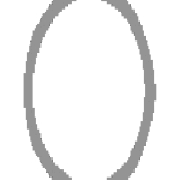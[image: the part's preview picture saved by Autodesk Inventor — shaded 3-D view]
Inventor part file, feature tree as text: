
AUTODESK INVENTOR PART (.ipt)
format: ipt  version: 2021 (Build 250183000, 183)  size: 113,152 bytes
history: native  units: in
note: dims shown in document units (in); Inventor stores cm internally (conversion verified against a paired STEP export)
features: other x4, sketch x3, plane x1
ambient origin geometry x8: Origin, YZ Plane, XZ Plane, XY Plane, X Axis, Y Axis, Z Axis, Center Point
bodies: Solid1 (feature_tree), Body (feature_tree)
feature tree (8):
  other  "Driven Length"
  other  "Frame Generator"
  other  "Start Plane"
  other  "End Plane"
  sketch  "Sketch"  dims[d2=13.5in d4=-0.0in d5=13.5in d6=0.12in d7=0.0in d8=90.0deg d9=13.5in]
  sketch  "Sketch2"  dims[d0=1.0in]
  plane  "Work Plane3"
  sketch  "Sketch3"  dims[d1=0.065in]
